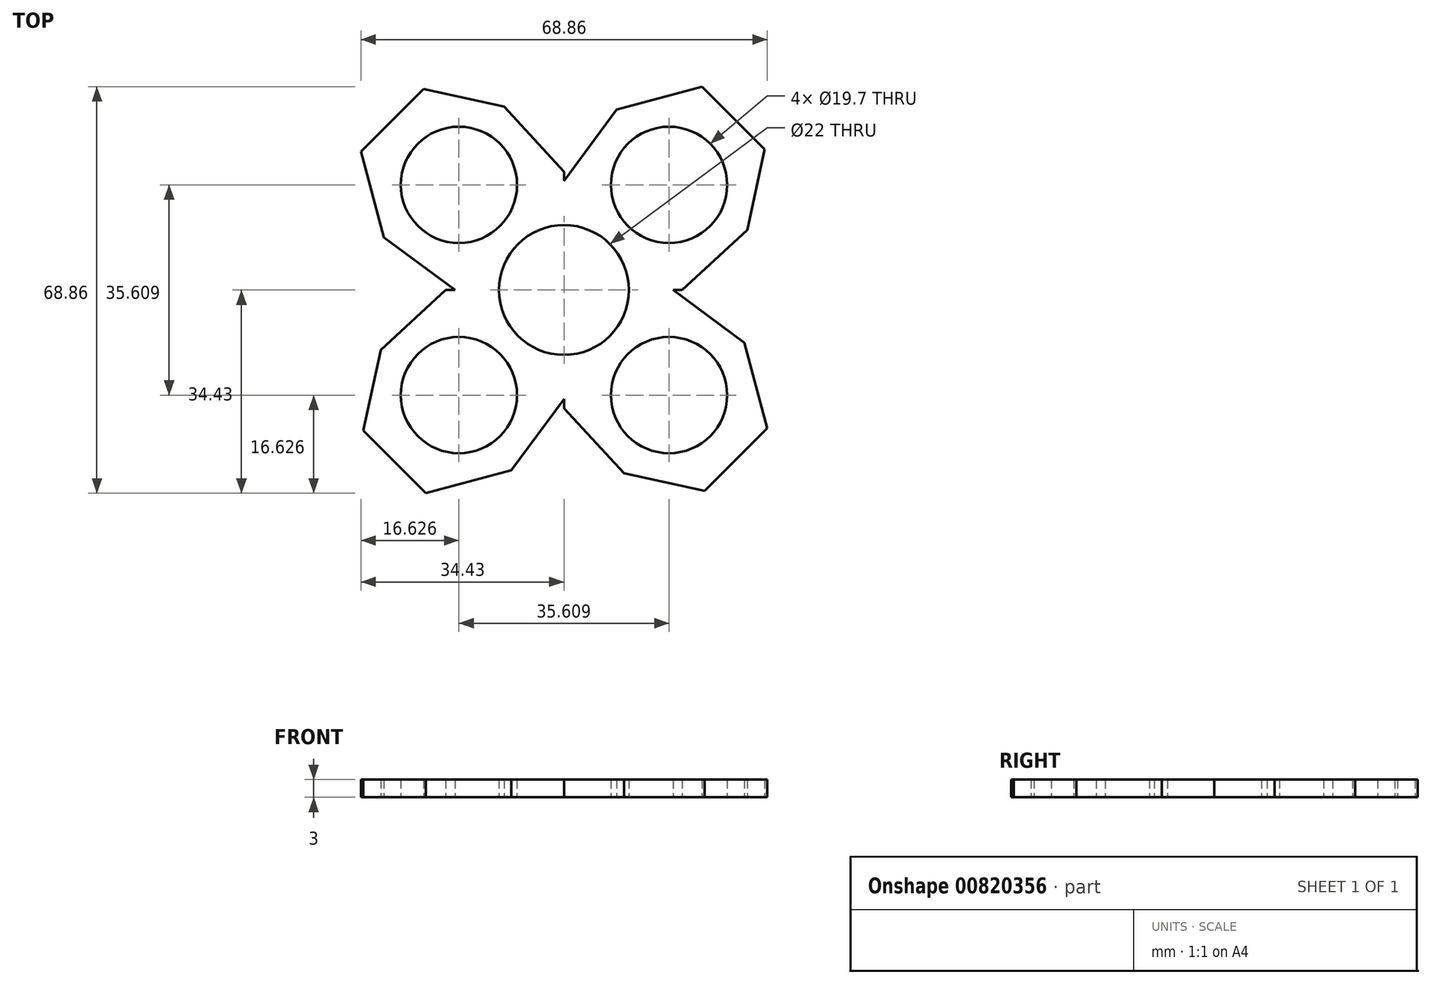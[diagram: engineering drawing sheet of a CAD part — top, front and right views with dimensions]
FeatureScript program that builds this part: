
annotation { "Feature Type Name" : "Feature", "Feature Type Description" : "" }
export const myFeature = defineFeature(function(context is Context, id is Id, definition is map)
    precondition{}
    {
        {
            var Q0;
            Q0=qCreatedBy(makeId("Top.planeOp"),FACE);
            var sketch = newSketch(context, id + "F0", { "sketchPlane" : qUnion([Q0])});
            skCircle(sketch, "E0", {"center": v(0, 0) * mm, "radius": 11 * mm});
            skCircle(sketch, "E1", {"center": v(-17.8, 17.8) * mm, "radius": 9.85 * mm});
            skLineSegment(sketch, "E2", {"start": v(-10.17, 31.05) * mm, "end": v(-23.82, 34.02) * mm});
            skLineSegment(sketch, "E3", {"start": v(-30.54, 8.92) * mm, "end": v(-34.43, 23.41) * mm});
            skLineSegment(sketch, "E4", {"start": v(-23.82, 34.02) * mm, "end": v(-34.43, 23.41) * mm});
            skLineSegment(sketch, "E5", {"start": v(-30.54, 8.92) * mm, "end": v(-18.49, 0) * mm});
            skLineSegment(sketch, "E6", {"start": v(-10.17, 31.05) * mm, "end": v(0, 20.03) * mm});
            skLineSegment(sketch, "E7.1.0", {"start": v(-31.05, -10.17) * mm, "end": v(-34.02, -23.82) * mm});
            skLineSegment(sketch, "E7.1.1", {"start": v(-8.92, -30.54) * mm, "end": v(0, -18.49) * mm});
            skLineSegment(sketch, "E7.1.2", {"start": v(-34.02, -23.82) * mm, "end": v(-23.41, -34.43) * mm});
            skLineSegment(sketch, "E7.1.3", {"start": v(-31.05, -10.17) * mm, "end": v(-20.03, 0) * mm});
            skLineSegment(sketch, "E7.1.5", {"start": v(-8.92, -30.54) * mm, "end": v(-23.41, -34.43) * mm});
            skCircle(sketch, "E7.1.6", {"center": v(-17.8, -17.8) * mm, "radius": 9.85 * mm});
            skLineSegment(sketch, "E7.2.0", {"start": v(10.17, -31.05) * mm, "end": v(23.82, -34.02) * mm});
            skLineSegment(sketch, "E7.2.1", {"start": v(30.54, -8.92) * mm, "end": v(18.49, 0) * mm});
            skLineSegment(sketch, "E7.2.2", {"start": v(23.82, -34.02) * mm, "end": v(34.43, -23.41) * mm});
            skLineSegment(sketch, "E7.2.3", {"start": v(10.17, -31.05) * mm, "end": v(0, -20.03) * mm});
            skLineSegment(sketch, "E7.2.5", {"start": v(30.54, -8.92) * mm, "end": v(34.43, -23.41) * mm});
            skCircle(sketch, "E7.2.6", {"center": v(17.8, -17.8) * mm, "radius": 9.85 * mm});
            skLineSegment(sketch, "E7.3.0", {"start": v(31.05, 10.17) * mm, "end": v(34.02, 23.82) * mm});
            skLineSegment(sketch, "E7.3.1", {"start": v(8.92, 30.54) * mm, "end": v(0, 18.49) * mm});
            skLineSegment(sketch, "E7.3.2", {"start": v(34.02, 23.82) * mm, "end": v(23.41, 34.43) * mm});
            skLineSegment(sketch, "E7.3.3", {"start": v(31.05, 10.17) * mm, "end": v(20.03, 0) * mm});
            skLineSegment(sketch, "E7.3.5", {"start": v(8.92, 30.54) * mm, "end": v(23.41, 34.43) * mm});
            skCircle(sketch, "E7.3.6", {"center": v(17.8, 17.8) * mm, "radius": 9.85 * mm});
            skLineSegment(sketch, "E8", {"start": v(-20.03, 0) * mm, "end": v(-18.49, 0) * mm});
            skLineSegment(sketch, "E9", {"start": v(0, -18.49) * mm, "end": v(0, -20.03) * mm});
            skLineSegment(sketch, "E10", {"start": v(20.03, 0) * mm, "end": v(18.49, 0) * mm});
            skLineSegment(sketch, "E11", {"start": v(0, 20.03) * mm, "end": v(0, 18.49) * mm});
            skSolve(sketch);
        }
        {
            var Q0;
            Q0 = qSketchRegion(id + "F0", true);
            extrude(context, id + "F1", {"entities" : qUnion([Q0]), "depth" : 3 * mm, "offsetDistance" : 25 * mm});
        }
    });
